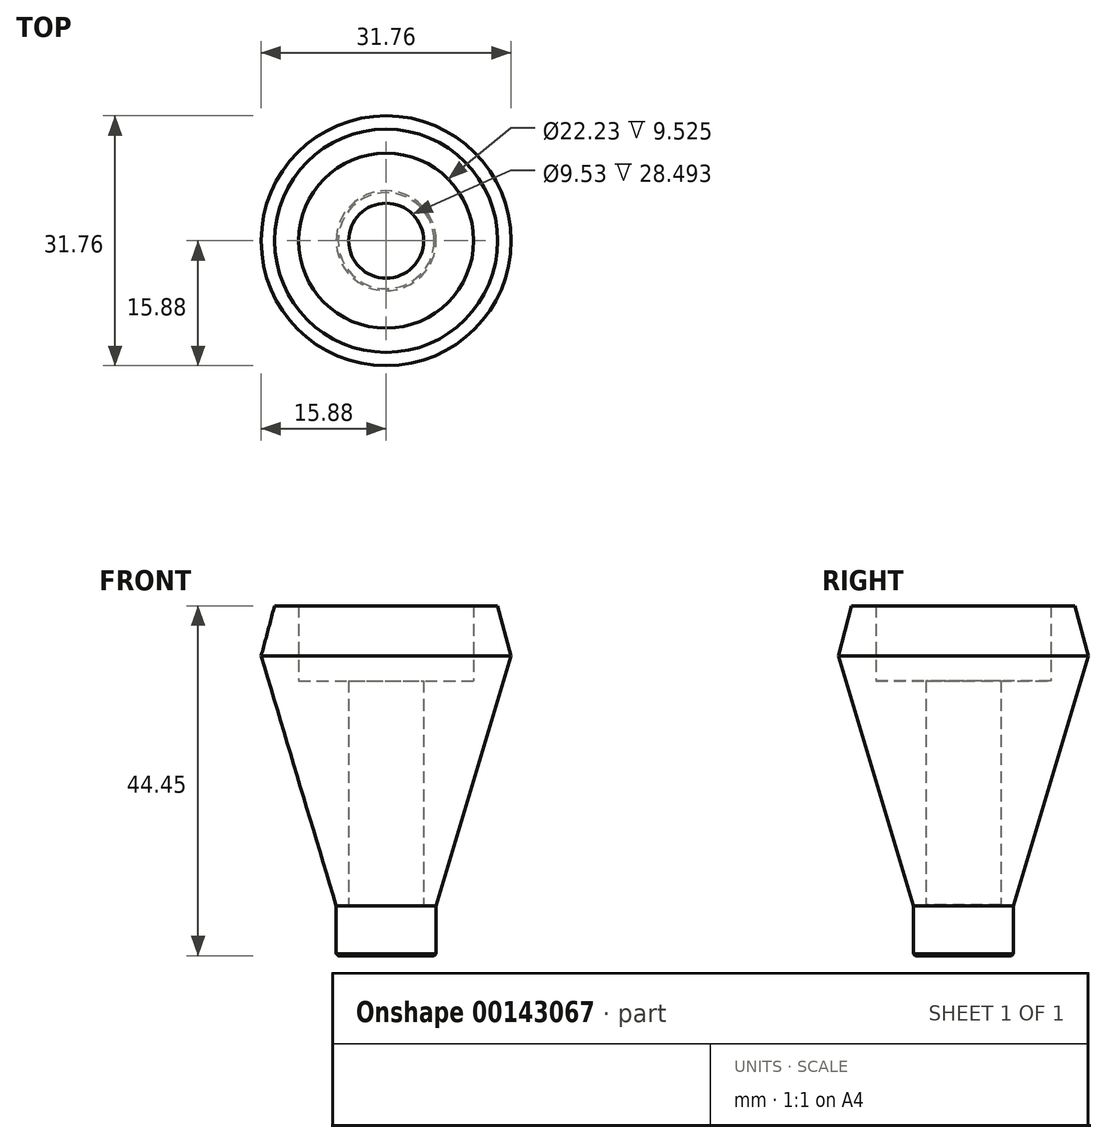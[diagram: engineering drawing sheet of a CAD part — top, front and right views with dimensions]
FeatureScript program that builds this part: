
annotation { "Feature Type Name" : "Feature", "Feature Type Description" : "" }
export const myFeature = defineFeature(function(context is Context, id is Id, definition is map)
    precondition{}
    {
        {
            var Q0;
            Q0=qCreatedBy(makeId("Front.planeOp"),FACE);
            var sketch = newSketch(context, id + "F0", { "sketchPlane" : qUnion([Q0])});
            skLineSegment(sketch, "E0", {"start": v(0, 0) * mm, "end": v(6.35, 0) * mm});
            skLineSegment(sketch, "E1", {"start": v(6.35, 0) * mm, "end": v(6.35, 6.35) * mm});
            skLineSegment(sketch, "E2", {"start": v(0, 0) * mm, "end": v(0, 38.1) * mm});
            skLineSegment(sketch, "E3", {"start": v(11.11, 44.45) * mm, "end": v(11.11, 34.93) * mm});
            skLineSegment(sketch, "E4", {"start": v(11.11, 34.93) * mm, "end": v(4.76, 34.93) * mm});
            skLineSegment(sketch, "E5", {"start": v(4.76, 34.93) * mm, "end": v(4.76, 6.43) * mm});
            skLineSegment(sketch, "E6", {"start": v(4.76, 6.43) * mm, "end": v(6.35, 6.35) * mm});
            skLineSegment(sketch, "E7", {"start": v(11.11, 38.1) * mm, "end": v(15.88, 38.1) * mm});
            skLineSegment(sketch, "E8", {"start": v(6.35, 6.35) * mm, "end": v(15.88, 38.1) * mm});
            skLineSegment(sketch, "E9", {"start": v(15.88, 38.1) * mm, "end": v(14.17, 44.45) * mm});
            skLineSegment(sketch, "E10", {"start": v(11.11, 44.45) * mm, "end": v(14.17, 44.45) * mm});
            skLineSegment(sketch, "E11", {"start": v(4.76, 6.43) * mm, "end": v(0, 6.43) * mm});
            skSolve(sketch);
        }
        {
            var Q0;
            {var subQ0=sQuery(id+"F0.wireOp",EDGE,"E4");Q0=makeQuery(id+"F0.imprint","IMPRINT",FACE,{"disambiguationData":[TD([[makeQuery(id+"F0.imprint","IMPRINT",EDGE,{"derivedFrom":subQ0}),1.0]])]});}
            var Q1;
            {var subQ1=sQuery(id+"F0.wireOp",EDGE,"E0");Q1=makeQuery(id+"F0.imprint","IMPRINT",FACE,{"disambiguationData":[TD([[makeQuery(id+"F0.imprint","IMPRINT",EDGE,{"derivedFrom":subQ1}),1.0]])]});}
            var Q2;
            {var subQ2=sQuery(id+"F0.wireOp",EDGE,"E7");Q2=makeQuery(id+"F0.imprint","IMPRINT",FACE,{"disambiguationData":[TD([[makeQuery(id+"F0.imprint","IMPRINT",EDGE,{"derivedFrom":subQ2}),1.0]])]});}
            var Q3;
            Q3=sQuery(id+"F0.wireOp",EDGE,"E2");
            revolve(context, id + "F1", {"entities" : qUnion([Q0, Q1, Q2]), "axis" : qUnion([Q3]), "revolveType" : RevolveType.FULL});
        }
        {
            var Q0;
            Q0=makeQuery(id+"F1.opRevolve","SWEPT_EDGE",EDGE,{"disambiguationData":[OSD([sQuery(id+"F0.wireOp",EDGE,"E0"),sQuery(id+"F0.wireOp",EDGE,"E1")])]});
            var Q1;
            Q1=makeQuery(id+"F1.opRevolve","SWEPT_FACE",FACE,{"disambiguationData":[OSD([sQuery(id+"F0.wireOp",EDGE,"E0")])]});
            chamfer(context, id + "F2", {"entities" : qUnion([Q0, Q1]), "chamferType" : ChamferType.OFFSET_ANGLE, "width" : 0.25 * mm, "oppositeDirection" : false, "angle" : 45 * degree, "tangentPropagation" : true});
        }
    });
